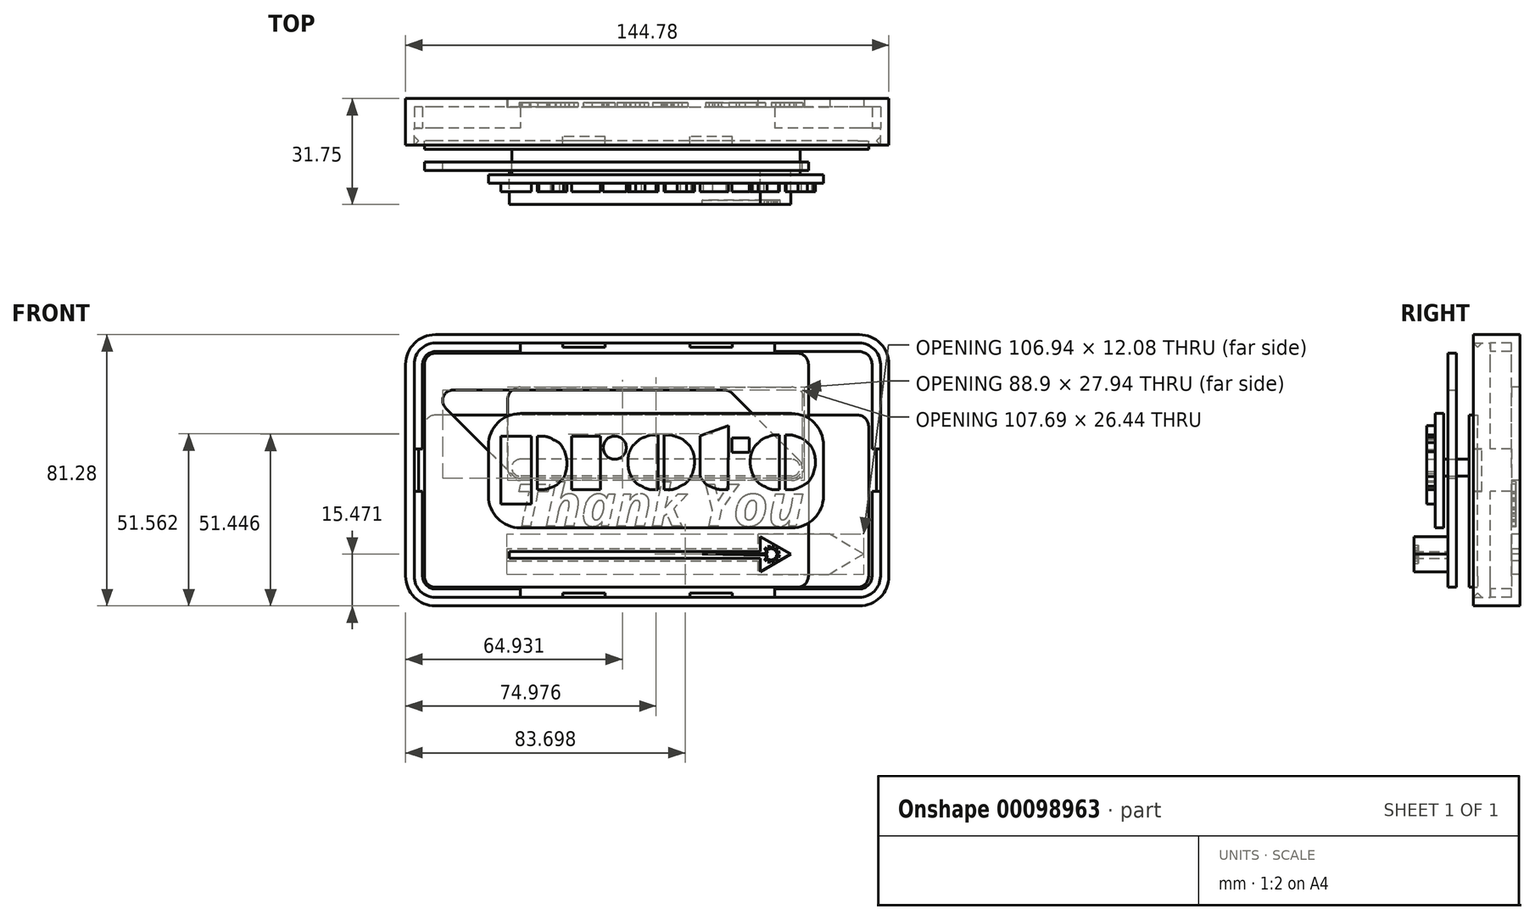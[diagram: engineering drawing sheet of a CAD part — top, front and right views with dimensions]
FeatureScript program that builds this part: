
annotation { "Feature Type Name" : "Feature", "Feature Type Description" : "" }
export const myFeature = defineFeature(function(context is Context, id is Id, definition is map)
    precondition{}
    {
        {
            var Q0;
            Q0=qCreatedBy(makeId("Front.planeOp"),FACE);
            var sketch = newSketch(context, id + "F0", { "sketchPlane" : qUnion([Q0])});
            skLineSegment(sketch, "E0", {"start": v(0, 0) * mm, "end": v(0, 76.06) * mm, "construction": true});
            skLineSegment(sketch, "E1", {"start": v(0, 0) * mm, "end": v(106.57, 0) * mm, "construction": true});
            skLineSegment(sketch, "E2.bottom", {"start": v(63.5, -38.1) * mm, "end": v(-63.5, -38.1) * mm});
            skLineSegment(sketch, "E2.top", {"start": v(63.5, 38.1) * mm, "end": v(-63.5, 38.1) * mm});
            skLineSegment(sketch, "E2.left", {"start": v(69.85, -31.75) * mm, "end": v(69.85, 31.75) * mm});
            skLineSegment(sketch, "E2.right", {"start": v(-69.85, -31.75) * mm, "end": v(-69.85, 31.75) * mm});
            skPoint(sketch, "E3.visualSharp", {"position": v(-69.85, 38.1) * mm});
            skArc(sketch, "E3.filletArc", {"start": v(-63.5, 38.1) * mm, "mid": v(-68, 36.24) * mm, "end": v(-69.85, 31.75) * mm});
            skPoint(sketch, "E4.visualSharp", {"position": v(69.85, 38.1) * mm});
            skArc(sketch, "E4.filletArc", {"start": v(69.85, 31.75) * mm, "mid": v(68, 36.24) * mm, "end": v(63.5, 38.1) * mm});
            skPoint(sketch, "E5.visualSharp", {"position": v(69.85, -38.1) * mm});
            skArc(sketch, "E5.filletArc", {"start": v(63.5, -38.1) * mm, "mid": v(68, -36.24) * mm, "end": v(69.85, -31.75) * mm});
            skPoint(sketch, "E6.visualSharp", {"position": v(-69.85, -38.1) * mm});
            skArc(sketch, "E6.filletArc", {"start": v(-69.85, -31.75) * mm, "mid": v(-68, -36.24) * mm, "end": v(-63.5, -38.1) * mm});
            skSolve(sketch);
        }
        {
            var Q0;
            Q0=makeQuery(id+"F0.imprint","IMPRINT",FACE,{"disambiguationData":[TD([[makeQuery(id+"F0.imprint","IMPRINT",EDGE,{"derivedFrom":sQuery(id+"F0.wireOp",EDGE,"E2.bottom")}),-1.0]])]});
            extrude(context, id + "F1", {"entities" : qUnion([Q0]), "depth" : 2.54 * mm});
        }
        {
            var Q0;
            Q0=makeQuery(id+"F1.opExtrude","CAP_FACE",FACE,{"disambiguationData":[OSD([sQuery(id+"F0.wireOp",EDGE,"E2.bottom"),sQuery(id+"F0.wireOp",EDGE,"E2.top"),sQuery(id+"F0.wireOp",EDGE,"E2.left"),sQuery(id+"F0.wireOp",EDGE,"E2.right"),sQuery(id+"F0.wireOp",EDGE,"E3.filletArc"),sQuery(id+"F0.wireOp",EDGE,"E4.filletArc"),sQuery(id+"F0.wireOp",EDGE,"E5.filletArc"),sQuery(id+"F0.wireOp",EDGE,"E6.filletArc")])],"isStart":false});
            var sketch = newSketch(context, id + "F2", { "sketchPlane" : qUnion([Q0])});
            skArc(sketch, "E7.0", {"start": v(67.31, 31.75) * mm, "mid": v(66.2, 34.44) * mm, "end": v(63.5, 35.56) * mm});
            skLineSegment(sketch, "E7.1", {"start": v(67.3, -31.75) * mm, "end": v(67.31, 31.75) * mm});
            skLineSegment(sketch, "E7.2", {"start": v(63.5, 35.56) * mm, "end": v(-63.5, 35.56) * mm});
            skArc(sketch, "E7.3", {"start": v(63.5, -35.56) * mm, "mid": v(66.2, -34.44) * mm, "end": v(67.3, -31.75) * mm});
            skArc(sketch, "E7.4", {"start": v(-63.5, 35.56) * mm, "mid": v(-66.2, 34.44) * mm, "end": v(-67.31, 31.75) * mm});
            skLineSegment(sketch, "E7.5", {"start": v(-67.31, -31.75) * mm, "end": v(-67.31, 31.75) * mm});
            skArc(sketch, "E7.6", {"start": v(-67.31, -31.75) * mm, "mid": v(-66.2, -34.44) * mm, "end": v(-63.5, -35.56) * mm});
            skLineSegment(sketch, "E7.7", {"start": v(63.5, -35.56) * mm, "end": v(-63.5, -35.56) * mm});
            skSolve(sketch);
        }
        {
            var Q0;
            Q0=makeQuery(id+"F2.imprint","IMPRINT",FACE,{"disambiguationData":[TD([[makeQuery(id+"F2.imprint","IMPRINT",EDGE,{"derivedFrom":sQuery(id+"F2.wireOp",EDGE,"E7.0")}),-1.0]])]});
            extrude(context, id + "F3", {"entities" : qUnion([Q0]), "operationType" : NewBodyOperationType.ADD, "depth" : 6.35 * mm});
        }
        {
            var Q0;
            Q0=qCreatedBy(makeId("Front.planeOp"),FACE);
            cPlane(context, id + "F4", {"entities" : qUnion([Q0]), "cplaneType" : CPlaneType.OFFSET, "offset" : 19.05 * mm, "width" : 152.4 * mm, "height" : 152.4 * mm});
        }
        {
            var Q0;
            Q0=qCreatedBy(id+"F4.planeOp",FACE);
            var sketch = newSketch(context, id + "F5", { "sketchPlane" : qUnion([Q0])});
            skLineSegment(sketch, "E8.0", {"start": v(44.96, -35.05) * mm, "end": v(-63.5, -35.05) * mm});
            skLineSegment(sketch, "E8.1", {"start": v(44.96, 35.05) * mm, "end": v(-63.5, 35.05) * mm});
            skArc(sketch, "E8.2", {"start": v(-63.5, 35.05) * mm, "mid": v(-65.83, 34.08) * mm, "end": v(-66.8, 31.75) * mm});
            skLineSegment(sketch, "E8.3", {"start": v(-66.8, -31.75) * mm, "end": v(-66.8, 31.75) * mm});
            skArc(sketch, "E8.4", {"start": v(-66.8, -31.75) * mm, "mid": v(-65.83, -34.08) * mm, "end": v(-63.5, -35.05) * mm});
            skLineSegment(sketch, "E9", {"start": v(48.26, 31.75) * mm, "end": v(48.26, -31.75) * mm});
            skPoint(sketch, "E10.visualSharp", {"position": v(48.26, 35.05) * mm});
            skArc(sketch, "E10.filletArc", {"start": v(48.26, 31.75) * mm, "mid": v(47.3, 34.08) * mm, "end": v(44.96, 35.05) * mm});
            skPoint(sketch, "E11.visualSharp", {"position": v(48.26, -35.05) * mm});
            skArc(sketch, "E11.filletArc", {"start": v(44.96, -35.05) * mm, "mid": v(47.3, -34.08) * mm, "end": v(48.26, -31.75) * mm});
            skLineSegment(sketch, "E12.left", {"start": v(-41.4, -26.43) * mm, "end": v(-41.4, -24.31) * mm});
            skPoint(sketch, "E13.endSnap0", {"position": v(48.26, 0) * mm});
            skLineSegment(sketch, "E14", {"start": v(-60.39, 18.6) * mm, "end": v(-40.3, -1.48) * mm});
            skLineSegment(sketch, "E15", {"start": v(-35.8, 3) * mm, "end": v(-55.9, 23.1) * mm});
            skArc(sketch, "E16", {"start": v(-40.3, -1.48) * mm, "mid": v(-35.8, -1.48) * mm, "end": v(-35.8, 3) * mm});
            skLineSegment(sketch, "E17.1.0.1", {"start": v(-15.49, 3) * mm, "end": v(-35.58, 23.1) * mm});
            skArc(sketch, "E17.1.0.3", {"start": v(-19.98, -1.48) * mm, "mid": v(-15.49, -1.48) * mm, "end": v(-15.49, 3) * mm});
            skLineSegment(sketch, "E17.1.0.6", {"start": v(-40.07, 18.6) * mm, "end": v(-19.98, -1.48) * mm});
            skLineSegment(sketch, "E17.2.0.1", {"start": v(4.83, 3) * mm, "end": v(-15.26, 23.1) * mm});
            skArc(sketch, "E17.2.0.3", {"start": v(0.34, -1.48) * mm, "mid": v(4.83, -1.48) * mm, "end": v(4.83, 3) * mm});
            skLineSegment(sketch, "E17.2.0.6", {"start": v(-19.75, 18.6) * mm, "end": v(0.34, -1.48) * mm});
            skLineSegment(sketch, "E18.1.3.0", {"start": v(25.15, 3) * mm, "end": v(5.06, 23.1) * mm});
            skArc(sketch, "E18.7.3.0", {"start": v(20.66, -1.48) * mm, "mid": v(25.15, -1.48) * mm, "end": v(25.15, 3) * mm});
            skLineSegment(sketch, "E18.15.3.0", {"start": v(0.57, 18.6) * mm, "end": v(20.66, -1.48) * mm});
            skLineSegment(sketch, "E18.1.4.0", {"start": v(45.47, 3) * mm, "end": v(25.38, 23.1) * mm});
            skArc(sketch, "E18.7.4.0", {"start": v(40.98, -1.48) * mm, "mid": v(45.47, -1.48) * mm, "end": v(45.47, 3) * mm});
            skLineSegment(sketch, "E18.15.4.0", {"start": v(20.9, 18.6) * mm, "end": v(40.98, -1.48) * mm});
            skArc(sketch, "E19", {"start": v(-55.9, 23.1) * mm, "mid": v(-60.39, 23.1) * mm, "end": v(-60.39, 18.6) * mm});
            skArc(sketch, "E20", {"start": v(-35.58, 23.1) * mm, "mid": v(-40.07, 23.1) * mm, "end": v(-40.07, 18.6) * mm});
            skArc(sketch, "E21", {"start": v(-15.26, 23.1) * mm, "mid": v(-19.75, 23.1) * mm, "end": v(-19.75, 18.6) * mm});
            skArc(sketch, "E22", {"start": v(5.06, 23.1) * mm, "mid": v(0.57, 23.1) * mm, "end": v(0.57, 18.6) * mm});
            skArc(sketch, "E23", {"start": v(25.38, 23.1) * mm, "mid": v(20.9, 23.1) * mm, "end": v(20.9, 18.6) * mm});
            skLineSegment(sketch, "E24", {"start": v(33.8, -30.45) * mm, "end": v(33.8, -26.43) * mm});
            skLineSegment(sketch, "E25", {"start": v(33.8, -26.43) * mm, "end": v(-41.4, -26.43) * mm});
            skLineSegment(sketch, "E26", {"start": v(-41.4, -24.31) * mm, "end": v(33.8, -24.31) * mm});
            skLineSegment(sketch, "E27", {"start": v(33.8, -24.31) * mm, "end": v(33.8, -19.9) * mm});
            skLineSegment(sketch, "E28", {"start": v(33.8, -19.9) * mm, "end": v(42.93, -25.17) * mm});
            skLineSegment(sketch, "E29", {"start": v(42.93, -25.17) * mm, "end": v(33.8, -30.45) * mm});
            skLineSegment(sketch, "E30", {"start": v(38.49, -25.17) * mm, "end": v(39.78, -24.46) * mm});
            skLineSegment(sketch, "E31", {"start": v(39.78, -24.46) * mm, "end": v(38.3, -24.48) * mm});
            skLineSegment(sketch, "E32", {"start": v(38.3, -24.48) * mm, "end": v(39.07, -23.21) * mm});
            skLineSegment(sketch, "E33", {"start": v(39.07, -23.21) * mm, "end": v(37.8, -23.97) * mm});
            skLineSegment(sketch, "E34", {"start": v(37.8, -23.97) * mm, "end": v(37.82, -22.5) * mm});
            skLineSegment(sketch, "E35", {"start": v(37.82, -22.5) * mm, "end": v(37.1, -23.78) * mm});
            skLineSegment(sketch, "E36", {"start": v(37.1, -23.78) * mm, "end": v(36.39, -22.49) * mm});
            skLineSegment(sketch, "E37", {"start": v(36.39, -22.49) * mm, "end": v(36.41, -23.97) * mm});
            skLineSegment(sketch, "E38", {"start": v(36.41, -23.97) * mm, "end": v(35.14, -23.2) * mm});
            skLineSegment(sketch, "E39", {"start": v(35.14, -23.2) * mm, "end": v(35.9, -24.47) * mm});
            skLineSegment(sketch, "E40", {"start": v(35.9, -24.47) * mm, "end": v(36.14, -24.84) * mm});
            skLineSegment(sketch, "E41", {"start": v(36.14, -24.84) * mm, "end": v(35.15, -24.85) * mm});
            skLineSegment(sketch, "E42", {"start": v(35.15, -24.85) * mm, "end": v(16.42, -25.17) * mm});
            skLineSegment(sketch, "E43", {"start": v(16.42, -25.17) * mm, "end": v(35.13, -25.5) * mm});
            skLineSegment(sketch, "E44", {"start": v(35.13, -25.5) * mm, "end": v(36.12, -25.5) * mm});
            skLineSegment(sketch, "E45", {"start": v(36.12, -25.5) * mm, "end": v(35.9, -25.86) * mm});
            skLineSegment(sketch, "E46", {"start": v(35.9, -25.86) * mm, "end": v(35.14, -27.13) * mm});
            skLineSegment(sketch, "E47", {"start": v(35.14, -27.13) * mm, "end": v(36.4, -26.37) * mm});
            skLineSegment(sketch, "E48", {"start": v(36.4, -26.37) * mm, "end": v(36.38, -27.85) * mm});
            skLineSegment(sketch, "E49", {"start": v(36.38, -27.85) * mm, "end": v(37.1, -26.56) * mm});
            skLineSegment(sketch, "E50", {"start": v(37.1, -26.56) * mm, "end": v(37.81, -27.85) * mm});
            skLineSegment(sketch, "E51", {"start": v(37.81, -27.85) * mm, "end": v(37.8, -26.37) * mm});
            skLineSegment(sketch, "E52", {"start": v(37.8, -26.37) * mm, "end": v(39.06, -27.14) * mm});
            skLineSegment(sketch, "E53", {"start": v(39.06, -27.14) * mm, "end": v(38.3, -25.87) * mm});
            skLineSegment(sketch, "E54", {"start": v(38.3, -25.87) * mm, "end": v(39.78, -25.9) * mm});
            skLineSegment(sketch, "E55", {"start": v(39.78, -25.9) * mm, "end": v(38.49, -25.17) * mm});
            skLineSegment(sketch, "E56", {"start": v(-58.14, 20.85) * mm, "end": v(-58.14, 24.03) * mm, "construction": true});
            skLineSegment(sketch, "E57", {"start": v(23.14, 20.85) * mm, "end": v(23.14, 24.03) * mm, "construction": true});
            skLineSegment(sketch, "E58", {"start": v(43.23, 0.76) * mm, "end": v(43.23, -2.41) * mm, "construction": true});
            skLineSegment(sketch, "E59", {"start": v(-38.05, 0.76) * mm, "end": v(-38.05, -2.41) * mm, "construction": true});
            skLineSegment(sketch, "E60", {"start": v(-58.14, 24.03) * mm, "end": v(23.14, 24.03) * mm});
            skLineSegment(sketch, "E61", {"start": v(43.23, -2.41) * mm, "end": v(-38.05, -2.41) * mm});
            skSolve(sketch);
        }
        {
            var Q0;
            Q0=makeQuery(id+"F5.imprint","IMPRINT",FACE,{"disambiguationData":[TD([[makeQuery(id+"F5.imprint","IMPRINT",EDGE,{"derivedFrom":sQuery(id+"F5.wireOp",EDGE,"E8.0")}),-1.0]])]});
            var Q1;
            Q1=makeQuery(id+"F5.imprint","IMPRINT",FACE,{"disambiguationData":[TD([[makeQuery(id+"F5.imprint","IMPRINT",EDGE,{"derivedFrom":sQuery(id+"F5.wireOp",EDGE,"E12.bottom")}),1.0]])]});
            var Q2;
            {var subQ0=sQuery(id+"F5.wireOp",EDGE,"RONYQzmz-jIdt-ileG-3skQ-5Jk7ZL3AeCge");Q2=makeQuery(id+"F5.imprint","IMPRINT",FACE,{"disambiguationData":[TD([[makeQuery(id+"F5.imprint","IMPRINT",EDGE,{"derivedFrom":subQ0}),-1.0]])]});}
            var Q3;
            {var subQ1=sQuery(id+"F5.wireOp",EDGE,"E17.1.0.2");Q3=makeQuery(id+"F5.imprint","IMPRINT",FACE,{"disambiguationData":[TD([[makeQuery(id+"F5.imprint","IMPRINT",EDGE,{"derivedFrom":subQ1}),-1.0]])]});}
            var Q4;
            {var subQ1=sQuery(id+"F5.wireOp",EDGE,"E17.2.0.2");Q4=makeQuery(id+"F5.imprint","IMPRINT",FACE,{"disambiguationData":[TD([[makeQuery(id+"F5.imprint","IMPRINT",EDGE,{"derivedFrom":subQ1}),-1.0]])]});}
            var Q5;
            {var subQ1=sQuery(id+"F5.wireOp",EDGE,"E18.4.3.0");Q5=makeQuery(id+"F5.imprint","IMPRINT",FACE,{"disambiguationData":[TD([[makeQuery(id+"F5.imprint","IMPRINT",EDGE,{"derivedFrom":subQ1}),-1.0]])]});}
            var Q6;
            {var subQ1=sQuery(id+"F5.wireOp",EDGE,"E18.4.4.0");Q6=makeQuery(id+"F5.imprint","IMPRINT",FACE,{"disambiguationData":[TD([[makeQuery(id+"F5.imprint","IMPRINT",EDGE,{"derivedFrom":subQ1}),-1.0]])]});}
            var Q7;
            Q7=makeQuery(id+"F5.imprint","IMPRINT",FACE,{"disambiguationData":[TD([[makeQuery(id+"F5.imprint","IMPRINT",EDGE,{"derivedFrom":sQuery(id+"F5.wireOp",EDGE,"E12.right")}),-1.0]])]});
            extrude(context, id + "F6", {"entities" : qUnion([Q0, Q1, Q2, Q3, Q4, Q5, Q6, Q7]), "depth" : 2.54 * mm});
        }
        {
            var Q0;
            Q0=makeQuery(id+"F5.imprint","IMPRINT",FACE,{"disambiguationData":[TD([[makeQuery(id+"F5.imprint","IMPRINT",EDGE,{"derivedFrom":sQuery(id+"F5.wireOp",EDGE,"E12.left")}),-1.0]])]});
            var Q1;
            Q1=makeQuery(id+"F5.imprint","IMPRINT",FACE,{"disambiguationData":[TD([[makeQuery(id+"F5.imprint","IMPRINT",EDGE,{"derivedFrom":sQuery(id+"F5.wireOp",EDGE,"E30")}),1.0]])]});
            extrude(context, id + "F7", {"entities" : qUnion([Q0, Q1]), "operationType" : NewBodyOperationType.ADD, "depth" : 12.7 * mm});
        }
        {
            var Q0;
            Q0=makeQuery(id+"F5.imprint","IMPRINT",FACE,{"disambiguationData":[TD([[makeQuery(id+"F5.imprint","IMPRINT",EDGE,{"derivedFrom":sQuery(id+"F5.wireOp",EDGE,"E30")}),1.0]])]});
            extrude(context, id + "F8", {"entities" : qUnion([Q0]), "operationType" : NewBodyOperationType.REMOVE, "endBound" : BoundingType.THROUGH_ALL, "depth" : 37.6 * mm, "hasSecondDirection" : true, "secondDirectionOppositeDirection" : false, "secondDirectionDepth" : 11.43 * mm});
        }
        {
            var Q0;
            Q0=qCreatedBy(makeId("Front.planeOp"),FACE);
            cPlane(context, id + "F9", {"entities" : qUnion([Q0]), "cplaneType" : CPlaneType.OFFSET, "offset" : 12.7 * mm, "width" : 152.4 * mm, "height" : 152.4 * mm});
        }
        {
            var Q0;
            Q0=qCreatedBy(id+"F9.planeOp",FACE);
            var sketch = newSketch(context, id + "F10", { "sketchPlane" : qUnion([Q0])});
            skLineSegment(sketch, "E62.0", {"start": v(-66.8, -31.75) * mm, "end": v(-66.8, 13.2) * mm});
            skLineSegment(sketch, "E62.1", {"start": v(63, -35.05) * mm, "end": v(-63.5, -35.05) * mm});
            skLineSegment(sketch, "E62.2", {"start": v(66.3, -31.75) * mm, "end": v(66.3, 13.2) * mm});
            skLineSegment(sketch, "E63", {"start": v(63, 16.5) * mm, "end": v(-63.5, 16.51) * mm});
            skArc(sketch, "E64.filletArc", {"start": v(-63.5, 16.51) * mm, "mid": v(-65.83, 15.54) * mm, "end": v(-66.8, 13.2) * mm});
            skArc(sketch, "E65.filletArc", {"start": v(66.3, 13.2) * mm, "mid": v(65.33, 15.54) * mm, "end": v(63, 16.5) * mm});
            skCircle(sketch, "E66", {"center": v(-38.05, 0.76) * mm, "radius": 2.54 * mm});
            skArc(sketch, "E67.0", {"start": v(-66.8, -31.75) * mm, "mid": v(-65.83, -34.08) * mm, "end": v(-63.5, -35.05) * mm});
            skPoint(sketch, "E68.visualSharp", {"position": v(66.3, -35.05) * mm});
            skArc(sketch, "E68.filletArc", {"start": v(63, -35.05) * mm, "mid": v(65.33, -34.08) * mm, "end": v(66.3, -31.75) * mm});
            skCircle(sketch, "E69", {"center": v(43.23, 0.76) * mm, "radius": 2.54 * mm});
            skLineSegment(sketch, "E70", {"start": v(-38.05, 3.3) * mm, "end": v(43.23, 3.3) * mm});
            skLineSegment(sketch, "E71", {"start": v(-38.05, -1.78) * mm, "end": v(43.23, -1.78) * mm});
            skSolve(sketch);
        }
        {
            var Q0;
            Q0=makeQuery(id+"F10.imprint","IMPRINT",FACE,{"disambiguationData":[TD([[makeQuery(id+"F10.imprint","IMPRINT",EDGE,{"derivedFrom":sQuery(id+"F10.wireOp",EDGE,"E62.0")}),-1.0]])]});
            var Q1;
            {var subQ0=sQuery(id+"F10.wireOp",EDGE,"E70");Q1=makeQuery(id+"F10.imprint","IMPRINT",FACE,{"disambiguationData":[TD([[makeQuery(id+"F10.imprint","IMPRINT",EDGE,{"derivedFrom":subQ0}),-1.0]])]});}
            var Q2;
            {var subQ0=sQuery(id+"F10.wireOp",EDGE,"E66");var subQ1=makeQuery(id+"F10.imprint","INTERSECT",VERTEX,{"derivedFrom":[subQ0,sQuery(id+"F10.wireOp",EDGE,"E70")]});Q2=makeQuery(id+"F10.imprint","IMPRINT",FACE,{"disambiguationData":[TD([[makeQuery(id+"F10.imprint","IMPRINT",EDGE,{"disambiguationData":[TD([[subQ1,-1.0]])],"derivedFrom":subQ0}),1.0]])]});}
            var Q3;
            {var subQ0=sQuery(id+"F10.wireOp",EDGE,"E69");var subQ1=makeQuery(id+"F10.imprint","INTERSECT",VERTEX,{"derivedFrom":[subQ0,sQuery(id+"F10.wireOp",EDGE,"E70")]});Q3=makeQuery(id+"F10.imprint","IMPRINT",FACE,{"disambiguationData":[TD([[makeQuery(id+"F10.imprint","IMPRINT",EDGE,{"disambiguationData":[TD([[subQ1,-1.0]])],"derivedFrom":subQ0}),1.0]])]});}
            extrude(context, id + "F11", {"entities" : qUnion([Q0, Q1, Q2, Q3]), "depth" : 2.54 * mm, "offsetDistance" : 25.4 * mm});
        }
        {
            var Q0;
            {var subQ0=sQuery(id+"F10.wireOp",EDGE,"E70");Q0=makeQuery(id+"F10.imprint","IMPRINT",FACE,{"disambiguationData":[TD([[makeQuery(id+"F10.imprint","IMPRINT",EDGE,{"derivedFrom":subQ0}),-1.0]])]});}
            var Q1;
            {var subQ0=sQuery(id+"F10.wireOp",EDGE,"E69");var subQ1=makeQuery(id+"F10.imprint","INTERSECT",VERTEX,{"derivedFrom":[subQ0,sQuery(id+"F10.wireOp",EDGE,"E70")]});Q1=makeQuery(id+"F10.imprint","IMPRINT",FACE,{"disambiguationData":[TD([[makeQuery(id+"F10.imprint","IMPRINT",EDGE,{"disambiguationData":[TD([[subQ1,-1.0]])],"derivedFrom":subQ0}),1.0]])]});}
            var Q2;
            {var subQ0=sQuery(id+"F10.wireOp",EDGE,"E66");var subQ1=makeQuery(id+"F10.imprint","INTERSECT",VERTEX,{"derivedFrom":[subQ0,sQuery(id+"F10.wireOp",EDGE,"E70")]});Q2=makeQuery(id+"F10.imprint","IMPRINT",FACE,{"disambiguationData":[TD([[makeQuery(id+"F10.imprint","IMPRINT",EDGE,{"disambiguationData":[TD([[subQ1,-1.0]])],"derivedFrom":subQ0}),1.0]])]});}
            extrude(context, id + "F12", {"entities" : qUnion([Q0, Q1, Q2]), "operationType" : NewBodyOperationType.ADD, "depth" : 10.16 * mm, "offsetDistance" : 25.4 * mm});
        }
        {
            var Q0;
            Q0=makeQuery(id+"F12.opExtrude","CAP_FACE",FACE,{"disambiguationData":[OSD([sQuery(id+"F10.wireOp",EDGE,"E66")])],"isStart":false});
            var sketch = newSketch(context, id + "F13", { "sketchPlane" : qUnion([Q0])});
            skArc(sketch, "E72", {"start": v(-38.05, 17.02) * mm, "mid": v(-44.79, 14.23) * mm, "end": v(-47.58, 7.5) * mm});
            skLineSegment(sketch, "E73", {"start": v(-47.58, 7.5) * mm, "end": v(-28.53, 7.5) * mm, "construction": true});
            skLineSegment(sketch, "E74", {"start": v(-47.58, -7.75) * mm, "end": v(-47.58, 7.5) * mm});
            skArc(sketch, "E75", {"start": v(-47.58, -7.75) * mm, "mid": v(-44.79, -14.48) * mm, "end": v(-38.05, -17.27) * mm});
            skArc(sketch, "E76", {"start": v(52.75, 7.5) * mm, "mid": v(49.96, 14.23) * mm, "end": v(43.23, 17.02) * mm});
            skLineSegment(sketch, "E77", {"start": v(52.75, 7.5) * mm, "end": v(52.75, -7.75) * mm});
            skArc(sketch, "E78", {"start": v(43.23, -17.27) * mm, "mid": v(49.96, -14.48) * mm, "end": v(52.75, -7.75) * mm});
            skLineSegment(sketch, "E79", {"start": v(-38.05, 17.02) * mm, "end": v(43.23, 17.02) * mm});
            skLineSegment(sketch, "E80", {"start": v(-38.05, -17.27) * mm, "end": v(43.23, -17.27) * mm});
            skSolve(sketch);
        }
        {
            var Q0;
            {var subQ2=sQuery(id+"F13.wireOp",EDGE,"184792f2-019b-4fa7-9458-c084a680c1f6.sketch_text.stroke-0");Q0=makeQuery(id+"F13.imprint","IMPRINT",FACE,{"disambiguationData":[TD([[makeQuery(id+"F13.imprint","IMPRINT",EDGE,{"derivedFrom":subQ2}),1.0]])]});}
            var Q1;
            {var subQ2=sQuery(id+"F13.wireOp",EDGE,"184792f2-019b-4fa7-9458-c084a680c1f6.sketch_text.stroke-0");Q1=makeQuery(id+"F13.imprint","IMPRINT",FACE,{"disambiguationData":[TD([[makeQuery(id+"F13.imprint","IMPRINT",EDGE,{"derivedFrom":subQ2}),-1.0]])]});}
            var Q2;
            {var subQ1=sQuery(id+"F13.wireOp",EDGE,"184792f2-019b-4fa7-9458-c084a680c1f6.sketch_text.stroke-3");Q2=makeQuery(id+"F13.imprint","IMPRINT",FACE,{"disambiguationData":[TD([[makeQuery(id+"F13.imprint","IMPRINT",EDGE,{"derivedFrom":subQ1}),1.0]])]});}
            var Q3;
            {var subQ10=sQuery(id+"F13.wireOp",EDGE,"184792f2-019b-4fa7-9458-c084a680c1f6.sketch_text.stroke-3");Q3=makeQuery(id+"F13.imprint","IMPRINT",FACE,{"disambiguationData":[TD([[makeQuery(id+"F13.imprint","IMPRINT",EDGE,{"derivedFrom":subQ10}),-1.0]])]});}
            var Q4;
            {var subQ0=sQuery(id+"F13.wireOp",EDGE,"184792f2-019b-4fa7-9458-c084a680c1f6.sketch_text.stroke-9");Q4=makeQuery(id+"F13.imprint","IMPRINT",FACE,{"disambiguationData":[TD([[makeQuery(id+"F13.imprint","IMPRINT",EDGE,{"derivedFrom":subQ0}),1.0]])]});}
            var Q5;
            Q5=makeQuery(id+"F13.imprint","IMPRINT",FACE,{"disambiguationData":[TD([[makeQuery(id+"F13.imprint","IMPRINT",EDGE,{"derivedFrom":sQuery(id+"F13.wireOp",EDGE,"E72")}),1.0]])]});
            var Q6;
            Q6=makeQuery(id+"F13.imprint","IMPRINT",FACE,{"disambiguationData":[TD([[makeQuery(id+"F13.imprint","IMPRINT",EDGE,{"derivedFrom":sQuery(id+"F13.wireOp",EDGE,"d38c979e-a2ed-44f1-b070-4af635d20e9c")}),1.0]])]});
            var Q7;
            Q7=makeQuery(id+"F13.imprint","IMPRINT",FACE,{"disambiguationData":[TD([[makeQuery(id+"F13.imprint","IMPRINT",EDGE,{"derivedFrom":sQuery(id+"F13.wireOp",EDGE,"0a407777-59e5-4105-bb9b-3a1e0d8dd915")}),1.0]])]});
            var Q8;
            Q8=makeQuery(id+"F13.imprint","IMPRINT",FACE,{"disambiguationData":[TD([[makeQuery(id+"F13.imprint","IMPRINT",EDGE,{"derivedFrom":sQuery(id+"F13.wireOp",EDGE,"69c1cf4b-b8d7-40c4-819d-392773c8632c")}),1.0]])]});
            var Q9;
            Q9=makeQuery(id+"F13.imprint","IMPRINT",FACE,{"disambiguationData":[TD([[makeQuery(id+"F13.imprint","IMPRINT",EDGE,{"derivedFrom":sQuery(id+"F13.wireOp",EDGE,"E76")}),1.0]])]});
            var Q10;
            Q10=makeQuery(id+"F13.imprint","IMPRINT",FACE,{"disambiguationData":[TD([[makeQuery(id+"F13.imprint","IMPRINT",EDGE,{"derivedFrom":makeQuery(id+"F12.opExtrude","CAP_EDGE",EDGE,{"disambiguationData":[OSD([sQuery(id+"F10.wireOp",EDGE,"E66")])],"isStart":false})}),1.0]])]});
            extrude(context, id + "F14", {"entities" : qUnion([Q0, Q1, Q2, Q3, Q4, Q5, Q6, Q7, Q8, Q9, Q10]), "depth" : 2.54 * mm});
        }
        {
            var Q0;
            Q0=makeQuery(id+"F14.opExtrude","CAP_FACE",FACE,{"disambiguationData":[OSD([sQuery(id+"F13.wireOp",EDGE,"E72"),sQuery(id+"F13.wireOp",EDGE,"E74"),sQuery(id+"F13.wireOp",EDGE,"E75"),sQuery(id+"F13.wireOp",EDGE,"E76"),sQuery(id+"F13.wireOp",EDGE,"E77"),sQuery(id+"F13.wireOp",EDGE,"E78"),sQuery(id+"F13.wireOp",EDGE,"E79"),sQuery(id+"F13.wireOp",EDGE,"E80")])],"isStart":false});
            var sketch = newSketch(context, id + "F15", { "sketchPlane" : qUnion([Q0])});
            skFitSpline(sketch, "E81", {"points": [v(39.38, -5.83) * mm, v(37.77, -5.83) * mm, v(36.3, -5.44) * mm, v(34.96, -4.73) * mm]});
            skFitSpline(sketch, "E82", {"points": [v(34.96, -4.73) * mm, v(33.65, -4.03) * mm, v(32.6, -3.04) * mm, v(31.84, -1.8) * mm]});
            skFitSpline(sketch, "E83", {"points": [v(31.34, 5.54) * mm, v(31.77, 6.52) * mm, v(32.38, 7.39) * mm, v(33.18, 8.15) * mm]});
            skFitSpline(sketch, "E84", {"points": [v(33.18, 8.15) * mm, v(33.98, 8.9) * mm, v(34.9, 9.54) * mm, v(35.93, 9.94) * mm]});
            skFitSpline(sketch, "E85", {"points": [v(35.93, 9.94) * mm, v(36.98, 10.34) * mm, v(38.1, 10.6) * mm, v(39.29, 10.6) * mm]});
            skFitSpline(sketch, "E86", {"points": [v(41.6, 10.6) * mm, v(42.9, 10.6) * mm, v(44.1, 10.35) * mm, v(45.18, 9.95) * mm]});
            skFitSpline(sketch, "E87", {"points": [v(45.18, 9.95) * mm, v(46.28, 9.55) * mm, v(47.22, 8.96) * mm, v(47.98, 8.24) * mm]});
            skFitSpline(sketch, "E88", {"points": [v(47.98, 8.24) * mm, v(48.78, 7.5) * mm, v(49.4, 6.62) * mm, v(49.83, 5.61) * mm]});
            skFitSpline(sketch, "E89", {"points": [v(49.35, -1.81) * mm, v(48.6, -3.04) * mm, v(47.55, -4.04) * mm, v(46.2, -4.75) * mm]});
            skFitSpline(sketch, "E90", {"points": [v(46.2, -4.75) * mm, v(44.87, -5.45) * mm, v(43.36, -5.83) * mm, v(41.68, -5.83) * mm]});
            skLineSegment(sketch, "E91", {"start": v(30.53, 5.41) * mm, "end": v(25.34, 5.41) * mm});
            skLineSegment(sketch, "E92", {"start": v(25.34, 5.41) * mm, "end": v(25.34, 9.74) * mm});
            skLineSegment(sketch, "E93", {"start": v(25.34, 9.74) * mm, "end": v(30.53, 9.74) * mm});
            skLineSegment(sketch, "E94", {"start": v(30.53, 9.74) * mm, "end": v(30.53, 5.41) * mm});
            skFitSpline(sketch, "E95", {"points": [v(5.35, 10.6) * mm, v(6.66, 10.6) * mm, v(7.85, 10.35) * mm, v(8.93, 9.95) * mm]});
            skFitSpline(sketch, "E96", {"points": [v(8.93, 9.95) * mm, v(10.03, 9.55) * mm, v(10.97, 8.96) * mm, v(11.73, 8.24) * mm]});
            skFitSpline(sketch, "E97", {"points": [v(11.73, 8.24) * mm, v(12.52, 7.5) * mm, v(13.14, 6.62) * mm, v(13.58, 5.61) * mm]});
            skFitSpline(sketch, "E98", {"points": [v(13.1, -1.81) * mm, v(12.35, -3.04) * mm, v(11.3, -4.04) * mm, v(9.95, -4.75) * mm]});
            skFitSpline(sketch, "E99", {"points": [v(9.95, -4.75) * mm, v(8.62, -5.45) * mm, v(7.1, -5.83) * mm, v(5.43, -5.83) * mm]});
            skFitSpline(sketch, "E100", {"points": [v(2.7, -5.83) * mm, v(1.09, -5.83) * mm, v(-0.39, -5.44) * mm, v(-1.72, -4.73) * mm]});
            skFitSpline(sketch, "E101", {"points": [v(-1.72, -4.73) * mm, v(-3.04, -4.03) * mm, v(-4.08, -3.04) * mm, v(-4.84, -1.8) * mm]});
            skFitSpline(sketch, "E102", {"points": [v(-5.34, 5.54) * mm, v(-4.92, 6.52) * mm, v(-4.3, 7.39) * mm, v(-3.5, 8.15) * mm]});
            skFitSpline(sketch, "E103", {"points": [v(-3.5, 8.15) * mm, v(-2.7, 8.9) * mm, v(-1.79, 9.54) * mm, v(-0.75, 9.94) * mm]});
            skFitSpline(sketch, "E104", {"points": [v(-0.75, 9.94) * mm, v(0.3, 10.34) * mm, v(1.41, 10.6) * mm, v(2.6, 10.6) * mm]});
            skFitSpline(sketch, "E105", {"points": [v(-32.57, 10.17) * mm, v(-31, 10.17) * mm, v(-29.54, 9.9) * mm, v(-28.2, 9.18) * mm]});
            skFitSpline(sketch, "E106", {"points": [v(-28.2, 9.18) * mm, v(-26.88, 8.48) * mm, v(-25.83, 7.55) * mm, v(-25.07, 6.3) * mm]});
            skFitSpline(sketch, "E107", {"points": [v(-24.53, -0.97) * mm, v(-24.93, -1.95) * mm, v(-25.5, -2.79) * mm, v(-26.23, -3.5) * mm]});
            skFitSpline(sketch, "E108", {"points": [v(-26.23, -3.5) * mm, v(-26.97, -4.24) * mm, v(-27.85, -4.79) * mm, v(-28.88, -5.18) * mm]});
            skFitSpline(sketch, "E109", {"points": [v(-28.88, -5.18) * mm, v(-29.9, -5.57) * mm, v(-31, -5.77) * mm, v(-32.22, -5.77) * mm]});
            skLineSegment(sketch, "E110", {"start": v(-43.83, -10.15) * mm, "end": v(-43.83, 10.17) * mm});
            skLineSegment(sketch, "E111", {"start": v(-43.83, 10.17) * mm, "end": v(-34.75, 10.17) * mm});
            skLineSegment(sketch, "E112", {"start": v(-34.75, 10.17) * mm, "end": v(-34.75, -10.15) * mm});
            skLineSegment(sketch, "E113", {"start": v(-34.75, -10.15) * mm, "end": v(-43.83, -10.15) * mm});
            skLineSegment(sketch, "E114", {"start": v(-14, -5.83) * mm, "end": v(-22.65, -5.83) * mm});
            skLineSegment(sketch, "E115", {"start": v(-22.65, -5.83) * mm, "end": v(-22.65, 10.17) * mm});
            skLineSegment(sketch, "E116", {"start": v(-22.65, 10.17) * mm, "end": v(-14, 10.17) * mm});
            skLineSegment(sketch, "E117", {"start": v(-14, 10.17) * mm, "end": v(-14, -5.83) * mm});
            skFitSpline(sketch, "E118", {"points": [v(23.68, -5.83) * mm, v(22.16, -5.83) * mm, v(20.8, -5.6) * mm, v(19.58, -5.12) * mm]});
            skFitSpline(sketch, "E119", {"points": [v(19.58, -5.12) * mm, v(18.33, -4.64) * mm, v(17.45, -4) * mm, v(16.79, -3.17) * mm]});
            skFitSpline(sketch, "E120", {"points": [v(16.79, -3.17) * mm, v(16.1, -2.34) * mm, v(15.83, -1.42) * mm, v(15.83, -0.4) * mm]});
            skLineSegment(sketch, "E121", {"start": v(15.83, -0.4) * mm, "end": v(15.83, 10.32) * mm});
            skLineSegment(sketch, "E122", {"start": v(15.83, 10.32) * mm, "end": v(24.33, 13.39) * mm});
            skLineSegment(sketch, "E123", {"start": v(24.33, 13.39) * mm, "end": v(24.23, -5.83) * mm});
            skLineSegment(sketch, "E124", {"start": v(24.23, -5.83) * mm, "end": v(23.68, -5.83) * mm});
            skLineSegment(sketch, "E125", {"start": v(-32.57, 10.17) * mm, "end": v(-33.02, 10.17) * mm});
            skLineSegment(sketch, "E126", {"start": v(-33.02, -5.83) * mm, "end": v(-32.61, -5.83) * mm});
            skLineSegment(sketch, "E127", {"start": v(-33.02, 10.17) * mm, "end": v(-33.02, -5.83) * mm});
            skLineSegment(sketch, "E128", {"start": v(-32.22, -5.77) * mm, "end": v(-32.61, -5.83) * mm});
            skArc(sketch, "E129", {"start": v(-24.53, -0.97) * mm, "mid": v(-24.12, 2.72) * mm, "end": v(-25.07, 6.3) * mm});
            skCircle(sketch, "E130", {"center": v(-9.75, 6.76) * mm, "radius": 3.46 * mm});
            skArc(sketch, "E131", {"start": v(-5.34, 5.54) * mm, "mid": v(-5.82, 1.83) * mm, "end": v(-4.84, -1.8) * mm});
            skArc(sketch, "E132", {"start": v(13.1, -1.81) * mm, "mid": v(14.12, 1.85) * mm, "end": v(13.58, 5.61) * mm});
            skLineSegment(sketch, "E133", {"start": v(3.3, 10.6) * mm, "end": v(3.3, -5.83) * mm});
            skLineSegment(sketch, "E134", {"start": v(5.02, -5.83) * mm, "end": v(5.02, 10.6) * mm});
            skLineSegment(sketch, "E135", {"start": v(2.6, 10.6) * mm, "end": v(3.3, 10.6) * mm});
            skLineSegment(sketch, "E136", {"start": v(5.02, 10.6) * mm, "end": v(5.35, 10.6) * mm});
            skLineSegment(sketch, "E137", {"start": v(2.7, -5.83) * mm, "end": v(3.3, -5.83) * mm});
            skLineSegment(sketch, "E138", {"start": v(5.02, -5.83) * mm, "end": v(5.43, -5.83) * mm});
            skLineSegment(sketch, "E139", {"start": v(39.6, 10.6) * mm, "end": v(39.6, -5.83) * mm});
            skLineSegment(sketch, "E140", {"start": v(41.34, -5.83) * mm, "end": v(41.34, 10.6) * mm});
            skLineSegment(sketch, "E141", {"start": v(39.29, 10.6) * mm, "end": v(39.6, 10.6) * mm});
            skLineSegment(sketch, "E142", {"start": v(41.34, 10.6) * mm, "end": v(41.6, 10.6) * mm});
            skLineSegment(sketch, "E143", {"start": v(39.38, -5.83) * mm, "end": v(39.6, -5.83) * mm});
            skLineSegment(sketch, "E144", {"start": v(41.34, -5.83) * mm, "end": v(41.68, -5.83) * mm});
            skArc(sketch, "E145", {"start": v(31.34, 5.54) * mm, "mid": v(30.83, 1.82) * mm, "end": v(31.84, -1.8) * mm});
            skArc(sketch, "E146", {"start": v(49.35, -1.81) * mm, "mid": v(50.33, 1.85) * mm, "end": v(49.83, 5.61) * mm});
            skSolve(sketch);
        }
        {
            var Q0;
            Q0=makeQuery(id+"F15.imprint","IMPRINT",FACE,{"disambiguationData":[TD([[makeQuery(id+"F15.imprint","IMPRINT",EDGE,{"derivedFrom":sQuery(id+"F15.wireOp",EDGE,"E110")}),-1.0]])]});
            var Q1;
            Q1=makeQuery(id+"F15.imprint","IMPRINT",FACE,{"disambiguationData":[TD([[makeQuery(id+"F15.imprint","IMPRINT",EDGE,{"derivedFrom":sQuery(id+"F15.wireOp",EDGE,"E105")}),-1.0]])]});
            var Q2;
            Q2=makeQuery(id+"F15.imprint","IMPRINT",FACE,{"disambiguationData":[TD([[makeQuery(id+"F15.imprint","IMPRINT",EDGE,{"derivedFrom":sQuery(id+"F15.wireOp",EDGE,"E114")}),-1.0]])]});
            var Q3;
            Q3=makeQuery(id+"F15.imprint","IMPRINT",FACE,{"disambiguationData":[TD([[makeQuery(id+"F15.imprint","IMPRINT",EDGE,{"derivedFrom":sQuery(id+"F15.wireOp",EDGE,"E130")}),1.0]])]});
            var Q4;
            Q4=makeQuery(id+"F15.imprint","IMPRINT",FACE,{"disambiguationData":[TD([[makeQuery(id+"F15.imprint","IMPRINT",EDGE,{"derivedFrom":sQuery(id+"F15.wireOp",EDGE,"E100")}),-1.0]])]});
            var Q5;
            Q5=makeQuery(id+"F15.imprint","IMPRINT",FACE,{"disambiguationData":[TD([[makeQuery(id+"F15.imprint","IMPRINT",EDGE,{"derivedFrom":sQuery(id+"F15.wireOp",EDGE,"E95")}),-1.0]])]});
            var Q6;
            Q6=makeQuery(id+"F15.imprint","IMPRINT",FACE,{"disambiguationData":[TD([[makeQuery(id+"F15.imprint","IMPRINT",EDGE,{"derivedFrom":sQuery(id+"F15.wireOp",EDGE,"E118")}),-1.0]])]});
            var Q7;
            Q7=makeQuery(id+"F15.imprint","IMPRINT",FACE,{"disambiguationData":[TD([[makeQuery(id+"F15.imprint","IMPRINT",EDGE,{"derivedFrom":sQuery(id+"F15.wireOp",EDGE,"E91")}),-1.0]])]});
            var Q8;
            Q8=makeQuery(id+"F15.imprint","IMPRINT",FACE,{"disambiguationData":[TD([[makeQuery(id+"F15.imprint","IMPRINT",EDGE,{"derivedFrom":sQuery(id+"F15.wireOp",EDGE,"E81")}),-1.0]])]});
            var Q9;
            Q9=makeQuery(id+"F15.imprint","IMPRINT",FACE,{"disambiguationData":[TD([[makeQuery(id+"F15.imprint","IMPRINT",EDGE,{"derivedFrom":sQuery(id+"F15.wireOp",EDGE,"E86")}),-1.0]])]});
            extrude(context, id + "F16", {"entities" : qUnion([Q0, Q1, Q2, Q3, Q4, Q5, Q6, Q7, Q8, Q9]), "operationType" : NewBodyOperationType.ADD, "depth" : 2.54 * mm});
        }
        {
            var Q0;
            Q0=makeQuery(id+"F0.imprint","IMPRINT",FACE,{"disambiguationData":[TD([[makeQuery(id+"F0.imprint","IMPRINT",EDGE,{"derivedFrom":sQuery(id+"F0.wireOp",EDGE,"E2.bottom")}),-1.0]])]});
            extrude(context, id + "F17", {"entities" : qUnion([Q0]), "depth" : 2.54 * mm});
        }
        {
            var Q0;
            Q0=makeQuery(id+"F17.opExtrude","CAP_FACE",FACE,{"disambiguationData":[OSD([sQuery(id+"F0.wireOp",EDGE,"E2.bottom"),sQuery(id+"F0.wireOp",EDGE,"E2.top"),sQuery(id+"F0.wireOp",EDGE,"E2.left"),sQuery(id+"F0.wireOp",EDGE,"E2.right"),sQuery(id+"F0.wireOp",EDGE,"E3.filletArc"),sQuery(id+"F0.wireOp",EDGE,"E4.filletArc"),sQuery(id+"F0.wireOp",EDGE,"E5.filletArc"),sQuery(id+"F0.wireOp",EDGE,"E6.filletArc")])],"isStart":false});
            var sketch = newSketch(context, id + "F18", { "sketchPlane" : qUnion([Q0])});
            skCircle(sketch, "E147.0", {"center": v(-38.05, 0.76) * mm, "radius": 2.54 * mm, "construction": true});
            skCircle(sketch, "E148.0", {"center": v(-17.73, 0.76) * mm, "radius": 2.54 * mm, "construction": true});
            skCircle(sketch, "E149.0", {"center": v(2.59, 0.76) * mm, "radius": 2.54 * mm, "construction": true});
            skCircle(sketch, "E150.0", {"center": v(22.9, 0.76) * mm, "radius": 2.54 * mm, "construction": true});
            skCircle(sketch, "E151.0", {"center": v(43.23, 0.76) * mm, "radius": 2.54 * mm, "construction": true});
            skLineSegment(sketch, "E152", {"start": v(-69.85, 0.76) * mm, "end": v(69.85, 0.76) * mm, "construction": true});
            skLineSegment(sketch, "E153", {"start": v(-69.85, 21.08) * mm, "end": v(69.85, 21.08) * mm, "construction": true});
            skArc(sketch, "E154", {"start": v(-41.86, 0.76) * mm, "mid": v(-38.05, -3.05) * mm, "end": v(-34.24, 0.76) * mm});
            skArc(sketch, "E155", {"start": v(-21.54, 0.76) * mm, "mid": v(-17.73, -3.05) * mm, "end": v(-13.92, 0.76) * mm});
            skArc(sketch, "E156", {"start": v(-1.22, 0.76) * mm, "mid": v(2.59, -3.05) * mm, "end": v(6.4, 0.76) * mm});
            skArc(sketch, "E157", {"start": v(19.1, 0.76) * mm, "mid": v(22.9, -3.05) * mm, "end": v(26.72, 0.76) * mm});
            skArc(sketch, "E158", {"start": v(39.42, 0.76) * mm, "mid": v(43.23, -3.05) * mm, "end": v(47.04, 0.76) * mm});
            skLineSegment(sketch, "E159", {"start": v(-41.86, 0.76) * mm, "end": v(-41.86, 21.08) * mm});
            skLineSegment(sketch, "E160", {"start": v(-34.24, 0.76) * mm, "end": v(-34.24, 21.08) * mm});
            skLineSegment(sketch, "E161", {"start": v(-21.54, 0.76) * mm, "end": v(-21.54, 21.08) * mm});
            skLineSegment(sketch, "E162", {"start": v(-13.92, 0.76) * mm, "end": v(-13.92, 21.08) * mm});
            skLineSegment(sketch, "E163", {"start": v(-1.22, 0.76) * mm, "end": v(-1.22, 21.08) * mm});
            skLineSegment(sketch, "E164", {"start": v(6.4, 0.76) * mm, "end": v(6.4, 21.08) * mm});
            skLineSegment(sketch, "E165", {"start": v(19.1, 0.76) * mm, "end": v(19.1, 21.08) * mm});
            skLineSegment(sketch, "E166", {"start": v(26.72, 0.76) * mm, "end": v(26.72, 21.08) * mm});
            skLineSegment(sketch, "E167", {"start": v(39.42, 0.76) * mm, "end": v(39.42, 21.08) * mm});
            skLineSegment(sketch, "E168", {"start": v(47.04, 0.76) * mm, "end": v(47.04, 21.08) * mm});
            skArc(sketch, "E169", {"start": v(-34.24, 21.08) * mm, "mid": v(-38.05, 24.9) * mm, "end": v(-41.86, 21.08) * mm});
            skArc(sketch, "E170", {"start": v(-13.92, 21.08) * mm, "mid": v(-17.73, 24.9) * mm, "end": v(-21.54, 21.08) * mm});
            skArc(sketch, "E171", {"start": v(6.4, 21.08) * mm, "mid": v(2.59, 24.9) * mm, "end": v(-1.22, 21.08) * mm});
            skArc(sketch, "E172", {"start": v(26.72, 21.08) * mm, "mid": v(22.9, 24.9) * mm, "end": v(19.1, 21.08) * mm});
            skArc(sketch, "E173", {"start": v(47.04, 21.08) * mm, "mid": v(43.23, 24.9) * mm, "end": v(39.42, 21.08) * mm});
            skLineSegment(sketch, "E174", {"start": v(33.03, -23.55) * mm, "end": v(-42.16, -23.55) * mm});
            skLineSegment(sketch, "E175", {"start": v(-42.16, -23.55) * mm, "end": v(-42.16, -27.2) * mm});
            skLineSegment(sketch, "E176", {"start": v(-42.16, -27.2) * mm, "end": v(33.03, -27.2) * mm});
            skLineSegment(sketch, "E177", {"start": v(33.03, -27.2) * mm, "end": v(33.03, -31.2) * mm});
            skLineSegment(sketch, "E178", {"start": v(33.03, -31.2) * mm, "end": v(64.78, -31.2) * mm});
            skLineSegment(sketch, "E179", {"start": v(64.78, -31.2) * mm, "end": v(64.78, -19.13) * mm});
            skLineSegment(sketch, "E180", {"start": v(64.78, -19.13) * mm, "end": v(33.03, -19.13) * mm});
            skLineSegment(sketch, "E181", {"start": v(33.03, -19.13) * mm, "end": v(33.03, -23.55) * mm});
            skLineSegment(sketch, "E182", {"start": v(64.78, -25.17) * mm, "end": v(54.62, -19.13) * mm});
            skLineSegment(sketch, "E183", {"start": v(64.78, -25.17) * mm, "end": v(54.62, -31.2) * mm});
            skLineSegment(sketch, "E184", {"start": v(-38.05, 24.9) * mm, "end": v(43.23, 24.9) * mm});
            skLineSegment(sketch, "E185", {"start": v(43.23, -3.05) * mm, "end": v(-38.05, -3.05) * mm});
            skSolve(sketch);
        }
        {
            var Q0;
            Q0=makeQuery(id+"F18.imprint","IMPRINT",FACE,{"disambiguationData":[TD([[makeQuery(id+"F18.imprint","IMPRINT",EDGE,{"derivedFrom":sQuery(id+"F18.wireOp",EDGE,"E154")}),1.0]])]});
            var Q1;
            Q1=makeQuery(id+"F18.imprint","IMPRINT",FACE,{"disambiguationData":[TD([[makeQuery(id+"F18.imprint","IMPRINT",EDGE,{"derivedFrom":sQuery(id+"F18.wireOp",EDGE,"E155")}),1.0]])]});
            var Q2;
            Q2=makeQuery(id+"F18.imprint","IMPRINT",FACE,{"disambiguationData":[TD([[makeQuery(id+"F18.imprint","IMPRINT",EDGE,{"derivedFrom":sQuery(id+"F18.wireOp",EDGE,"E156")}),1.0]])]});
            var Q3;
            Q3=makeQuery(id+"F18.imprint","IMPRINT",FACE,{"disambiguationData":[TD([[makeQuery(id+"F18.imprint","IMPRINT",EDGE,{"derivedFrom":sQuery(id+"F18.wireOp",EDGE,"E157")}),1.0]])]});
            var Q4;
            Q4=makeQuery(id+"F18.imprint","IMPRINT",FACE,{"disambiguationData":[TD([[makeQuery(id+"F18.imprint","IMPRINT",EDGE,{"derivedFrom":sQuery(id+"F18.wireOp",EDGE,"E158")}),1.0]])]});
            var Q5;
            Q5=makeQuery(id+"F18.imprint","IMPRINT",FACE,{"disambiguationData":[TD([[makeQuery(id+"F18.imprint","IMPRINT",EDGE,{"derivedFrom":sQuery(id+"F18.wireOp",EDGE,"E174")}),1.0]])]});
            var Q6;
            {var subQ1=sQuery(id+"F18.wireOp",EDGE,"E160");Q6=makeQuery(id+"F18.imprint","IMPRINT",FACE,{"disambiguationData":[TD([[makeQuery(id+"F18.imprint","IMPRINT",EDGE,{"derivedFrom":subQ1}),-1.0]])]});}
            var Q7;
            {var subQ1=sQuery(id+"F18.wireOp",EDGE,"E162");Q7=makeQuery(id+"F18.imprint","IMPRINT",FACE,{"disambiguationData":[TD([[makeQuery(id+"F18.imprint","IMPRINT",EDGE,{"derivedFrom":subQ1}),-1.0]])]});}
            var Q8;
            {var subQ1=sQuery(id+"F18.wireOp",EDGE,"E164");Q8=makeQuery(id+"F18.imprint","IMPRINT",FACE,{"disambiguationData":[TD([[makeQuery(id+"F18.imprint","IMPRINT",EDGE,{"derivedFrom":subQ1}),-1.0]])]});}
            var Q9;
            {var subQ1=sQuery(id+"F18.wireOp",EDGE,"E166");Q9=makeQuery(id+"F18.imprint","IMPRINT",FACE,{"disambiguationData":[TD([[makeQuery(id+"F18.imprint","IMPRINT",EDGE,{"derivedFrom":subQ1}),-1.0]])]});}
            extrude(context, id + "F19", {"entities" : qUnion([Q0, Q1, Q2, Q3, Q4, Q5, Q6, Q7, Q8, Q9]), "operationType" : NewBodyOperationType.REMOVE, "endBound" : BoundingType.UP_TO_NEXT, "oppositeDirection" : true, "depth" : 25.4 * mm, "offsetDistance" : 25.4 * mm});
        }
        {
            var Q0;
            Q0=makeQuery(id+"F17.opExtrude","CAP_FACE",FACE,{"disambiguationData":[OSD([sQuery(id+"F0.wireOp",EDGE,"E2.bottom"),sQuery(id+"F0.wireOp",EDGE,"E2.top"),sQuery(id+"F0.wireOp",EDGE,"E2.left"),sQuery(id+"F0.wireOp",EDGE,"E2.right"),sQuery(id+"F0.wireOp",EDGE,"E3.filletArc"),sQuery(id+"F0.wireOp",EDGE,"E4.filletArc"),sQuery(id+"F0.wireOp",EDGE,"E5.filletArc"),sQuery(id+"F0.wireOp",EDGE,"E6.filletArc")])],"isStart":false});
            var sketch = newSketch(context, id + "F20", { "sketchPlane" : qUnion([Q0])});
            skText(sketch, "E186", { "text": "Thank You", "fontName": "OpenSans-BoldItalic.ttf"});
            const initialGuessF20  = {"E186": [-0.03988, -0.01676, 1, 0, 0.0127]};
            skSetInitialGuess(sketch, initialGuessF20);
            skSolve(sketch);
        }
        {
            var Q0;
            Q0 = qSketchRegion(id + "F20", true);
            extrude(context, id + "F21", {"entities" : qUnion([Q0]), "operationType" : NewBodyOperationType.REMOVE, "oppositeDirection" : true, "depth" : 1.27 * mm});
        }
        {
            var Q0;
            Q0=qCreatedBy(makeId("Right.planeOp"),FACE);
            var sketch = newSketch(context, id + "F22", { "sketchPlane" : qUnion([Q0])});
            skLineSegment(sketch, "E187.0", {"start": v(-8.9, 38.1) * mm, "end": v(0, 38.1) * mm});
            skLineSegment(sketch, "E188.0", {"start": v(0, 31.75) * mm, "end": v(0, 38.1) * mm});
            skLineSegment(sketch, "E189.0", {"start": v(-8.9, 31.75) * mm, "end": v(-8.9, 38.1) * mm});
            skLineSegment(sketch, "E190", {"start": v(0, 38.1) * mm, "end": v(0, 40.64) * mm});
            skLineSegment(sketch, "E191", {"start": v(0, 40.64) * mm, "end": v(-13.97, 40.64) * mm});
            skLineSegment(sketch, "E192", {"start": v(-13.97, 40.64) * mm, "end": v(-13.97, 38.1) * mm});
            skLineSegment(sketch, "E193", {"start": v(-13.97, 38.1) * mm, "end": v(-12.7, 36.83) * mm});
            skLineSegment(sketch, "E194", {"start": v(-12.7, 36.83) * mm, "end": v(-11.43, 38.1) * mm});
            skLineSegment(sketch, "E195", {"start": v(-11.43, 38.1) * mm, "end": v(-8.9, 38.1) * mm});
            skSolve(sketch);
        }
        {
            var Q0;
            Q0=makeQuery(id+"F1.opExtrude","CAP_FACE",FACE,{"disambiguationData":[OSD([sQuery(id+"F0.wireOp",EDGE,"E2.bottom"),sQuery(id+"F0.wireOp",EDGE,"E2.top"),sQuery(id+"F0.wireOp",EDGE,"E2.left"),sQuery(id+"F0.wireOp",EDGE,"E2.right"),sQuery(id+"F0.wireOp",EDGE,"E3.filletArc"),sQuery(id+"F0.wireOp",EDGE,"E4.filletArc"),sQuery(id+"F0.wireOp",EDGE,"E5.filletArc"),sQuery(id+"F0.wireOp",EDGE,"E6.filletArc")])],"isStart":true});
            var sketch = newSketch(context, id + "F23", { "sketchPlane" : qUnion([Q0])});
            skLineSegment(sketch, "E196", {"start": v(0, 38.1) * mm, "end": v(63.5, 38.1) * mm});
            skArc(sketch, "E197.0", {"start": v(63.5, 38.1) * mm, "mid": v(68, 36.24) * mm, "end": v(69.85, 31.75) * mm});
            skLineSegment(sketch, "E198.0", {"start": v(69.85, -31.75) * mm, "end": v(69.85, 31.75) * mm});
            skArc(sketch, "E199.0", {"start": v(69.85, -31.75) * mm, "mid": v(68, -36.24) * mm, "end": v(63.5, -38.1) * mm});
            skLineSegment(sketch, "E200.0", {"start": v(-63.5, -38.1) * mm, "end": v(63.5, -38.1) * mm});
            skArc(sketch, "E201.0", {"start": v(-63.5, -38.1) * mm, "mid": v(-68, -36.24) * mm, "end": v(-69.85, -31.75) * mm});
            skLineSegment(sketch, "E202.0", {"start": v(-69.85, -31.75) * mm, "end": v(-69.85, 31.75) * mm});
            skArc(sketch, "E203.0", {"start": v(-69.85, 31.75) * mm, "mid": v(-68, 36.24) * mm, "end": v(-63.5, 38.1) * mm});
            skLineSegment(sketch, "E204", {"start": v(-63.5, 38.1) * mm, "end": v(0, 38.1) * mm});
            skSolve(sketch);
        }
        {
            var Q0;
            Q0=makeQuery(id+"F22.imprint","IMPRINT",FACE,{"disambiguationData":[TD([[makeQuery(id+"F22.imprint","IMPRINT",EDGE,{"derivedFrom":sQuery(id+"F22.wireOp",EDGE,"E187.0")}),1.0]])]});
            var Q1;
            Q1 = qConstructionFilter(qBodyType(qCreatedBy(id + "F23" ,EDGE), BodyType.WIRE), ConstructionObject.NO);
            sweep(context, id + "F24", {"operationType" : NewBodyOperationType.ADD, "profiles" : qUnion([Q0]), "path" : qUnion([Q1])});
        }
        {
            var Q0;
            Q0=makeQuery(id+"F3.opExtrude","CAP_FACE",FACE,{"disambiguationData":[OSD([sQuery(id+"F0.wireOp",EDGE,"E2.bottom"),sQuery(id+"F0.wireOp",EDGE,"E2.top"),sQuery(id+"F0.wireOp",EDGE,"E2.left"),sQuery(id+"F0.wireOp",EDGE,"E2.right"),sQuery(id+"F0.wireOp",EDGE,"E3.filletArc"),sQuery(id+"F0.wireOp",EDGE,"E4.filletArc"),sQuery(id+"F0.wireOp",EDGE,"E5.filletArc"),sQuery(id+"F0.wireOp",EDGE,"E6.filletArc"),sQuery(id+"F2.wireOp",EDGE,"E7.0"),sQuery(id+"F2.wireOp",EDGE,"E7.1"),sQuery(id+"F2.wireOp",EDGE,"E7.2"),sQuery(id+"F2.wireOp",EDGE,"E7.3"),sQuery(id+"F2.wireOp",EDGE,"E7.4"),sQuery(id+"F2.wireOp",EDGE,"E7.5"),sQuery(id+"F2.wireOp",EDGE,"E7.6"),sQuery(id+"F2.wireOp",EDGE,"E7.7")])],"isStart":false});
            var sketch = newSketch(context, id + "F25", { "sketchPlane" : qUnion([Q0])});
            skLineSegment(sketch, "E205.0", {"start": v(63.5, 38.1) * mm, "end": v(-63.5, 38.1) * mm});
            skLineSegment(sketch, "E206.0", {"start": v(-69.85, -31.75) * mm, "end": v(-69.85, 31.75) * mm});
            skLineSegment(sketch, "E207.0", {"start": v(63.5, -38.1) * mm, "end": v(-63.5, -38.1) * mm});
            skLineSegment(sketch, "E208.0", {"start": v(69.85, -31.75) * mm, "end": v(69.85, 31.75) * mm});
            skLineSegment(sketch, "E209", {"start": v(-12.7, 38.1) * mm, "end": v(-12.7, -38.1) * mm});
            skLineSegment(sketch, "E210", {"start": v(-25.4, 38.1) * mm, "end": v(-25.4, -38.1) * mm});
            skLineSegment(sketch, "E211", {"start": v(-38.1, 38.1) * mm, "end": v(-38.1, -38.1) * mm});
            skLineSegment(sketch, "E212", {"start": v(-50.8, 38.1) * mm, "end": v(-50.8, -38.1) * mm});
            skLineSegment(sketch, "E213", {"start": v(-69.85, 6.35) * mm, "end": v(69.85, 6.35) * mm});
            skLineSegment(sketch, "E214", {"start": v(-75.27, 0) * mm, "end": v(78.66, 0) * mm, "construction": true});
            skLineSegment(sketch, "E215", {"start": v(0, 56.55) * mm, "end": v(0, -47.98) * mm, "construction": true});
            skLineSegment(sketch, "E216.MirrorCS", {"start": v(-69.85, -6.35) * mm, "end": v(69.85, -6.35) * mm});
            skLineSegment(sketch, "E217.MirrorCS", {"start": v(12.7, 38.1) * mm, "end": v(12.7, -38.1) * mm});
            skLineSegment(sketch, "E218.MirrorCS", {"start": v(25.4, 38.1) * mm, "end": v(25.4, -38.1) * mm});
            skLineSegment(sketch, "E219.MirrorCS", {"start": v(38.1, 38.1) * mm, "end": v(38.1, -38.1) * mm});
            skLineSegment(sketch, "E220.MirrorCS", {"start": v(50.8, 38.1) * mm, "end": v(50.8, -38.1) * mm});
            skSolve(sketch);
        }
        {
            var Q0;
            {var subQ5=makeQuery(id+"F3.opExtrude","CAP_EDGE",EDGE,{"disambiguationData":[OSD([sQuery(id+"F2.wireOp",EDGE,"E7.4")])],"isStart":false});Q0=makeQuery(id+"F25.imprint","IMPRINT",FACE,{"disambiguationData":[TD([[makeQuery(id+"F25.imprint","IMPRINT",EDGE,{"derivedFrom":subQ5}),-1.0]])]});}
            var Q1;
            {var subQ0=sQuery(id+"F25.wireOp",EDGE,"E210");var subQ1=sQuery(id+"F25.wireOp",EDGE,"E205.0");var subQ2=makeQuery(id+"F25.imprint","INTERSECT",VERTEX,{"derivedFrom":[subQ1,subQ0]});Q1=makeQuery(id+"F25.imprint","IMPRINT",FACE,{"disambiguationData":[TD([[makeQuery(id+"F25.imprint","IMPRINT",EDGE,{"disambiguationData":[TD([[subQ2,-1.0]])],"derivedFrom":subQ1}),1.0]])]});}
            var Q2;
            {var subQ0=sQuery(id+"F25.wireOp",EDGE,"E209");var subQ1=sQuery(id+"F25.wireOp",EDGE,"E205.0");var subQ2=makeQuery(id+"F25.imprint","INTERSECT",VERTEX,{"derivedFrom":[subQ1,subQ0]});Q2=makeQuery(id+"F25.imprint","IMPRINT",FACE,{"disambiguationData":[TD([[makeQuery(id+"F25.imprint","IMPRINT",EDGE,{"disambiguationData":[TD([[subQ2,1.0]])],"derivedFrom":subQ1}),1.0]])]});}
            var Q3;
            {var subQ0=sQuery(id+"F25.wireOp",EDGE,"E218.MirrorCS");var subQ1=sQuery(id+"F25.wireOp",EDGE,"E205.0");var subQ2=makeQuery(id+"F25.imprint","INTERSECT",VERTEX,{"derivedFrom":[subQ1,subQ0]});Q3=makeQuery(id+"F25.imprint","IMPRINT",FACE,{"disambiguationData":[TD([[makeQuery(id+"F25.imprint","IMPRINT",EDGE,{"disambiguationData":[TD([[subQ2,1.0]])],"derivedFrom":subQ1}),1.0]])]});}
            var Q4;
            {var subQ11=makeQuery(id+"F3.opExtrude","CAP_EDGE",EDGE,{"disambiguationData":[OSD([sQuery(id+"F2.wireOp",EDGE,"E7.0")])],"isStart":false});Q4=makeQuery(id+"F25.imprint","IMPRINT",FACE,{"disambiguationData":[TD([[makeQuery(id+"F25.imprint","IMPRINT",EDGE,{"derivedFrom":subQ11}),-1.0]])]});}
            var Q5;
            {var subQ11=makeQuery(id+"F3.opExtrude","CAP_EDGE",EDGE,{"disambiguationData":[OSD([sQuery(id+"F2.wireOp",EDGE,"E7.3")])],"isStart":false});Q5=makeQuery(id+"F25.imprint","IMPRINT",FACE,{"disambiguationData":[TD([[makeQuery(id+"F25.imprint","IMPRINT",EDGE,{"derivedFrom":subQ11}),-1.0]])]});}
            var Q6;
            {var subQ0=sQuery(id+"F25.wireOp",EDGE,"E218.MirrorCS");var subQ1=sQuery(id+"F25.wireOp",EDGE,"E207.0");var subQ2=makeQuery(id+"F25.imprint","INTERSECT",VERTEX,{"derivedFrom":[subQ1,subQ0]});Q6=makeQuery(id+"F25.imprint","IMPRINT",FACE,{"disambiguationData":[TD([[makeQuery(id+"F25.imprint","IMPRINT",EDGE,{"disambiguationData":[TD([[subQ2,1.0]])],"derivedFrom":subQ1}),-1.0]])]});}
            var Q7;
            {var subQ0=sQuery(id+"F25.wireOp",EDGE,"E209");var subQ1=sQuery(id+"F25.wireOp",EDGE,"E207.0");var subQ2=makeQuery(id+"F25.imprint","INTERSECT",VERTEX,{"derivedFrom":[subQ1,subQ0]});Q7=makeQuery(id+"F25.imprint","IMPRINT",FACE,{"disambiguationData":[TD([[makeQuery(id+"F25.imprint","IMPRINT",EDGE,{"disambiguationData":[TD([[subQ2,1.0]])],"derivedFrom":subQ1}),-1.0]])]});}
            var Q8;
            {var subQ0=sQuery(id+"F25.wireOp",EDGE,"E210");var subQ1=sQuery(id+"F25.wireOp",EDGE,"E207.0");var subQ2=makeQuery(id+"F25.imprint","INTERSECT",VERTEX,{"derivedFrom":[subQ1,subQ0]});Q8=makeQuery(id+"F25.imprint","IMPRINT",FACE,{"disambiguationData":[TD([[makeQuery(id+"F25.imprint","IMPRINT",EDGE,{"disambiguationData":[TD([[subQ2,-1.0]])],"derivedFrom":subQ1}),-1.0]])]});}
            var Q9;
            {var subQ11=makeQuery(id+"F3.opExtrude","CAP_EDGE",EDGE,{"disambiguationData":[OSD([sQuery(id+"F2.wireOp",EDGE,"E7.6")])],"isStart":false});Q9=makeQuery(id+"F25.imprint","IMPRINT",FACE,{"disambiguationData":[TD([[makeQuery(id+"F25.imprint","IMPRINT",EDGE,{"derivedFrom":subQ11}),-1.0]])]});}
            var Q10;
            {var subQ0=sQuery(id+"F25.wireOp",EDGE,"E211");var subQ1=sQuery(id+"F25.wireOp",EDGE,"E205.0");var subQ2=makeQuery(id+"F25.imprint","INTERSECT",VERTEX,{"derivedFrom":[subQ1,subQ0]});Q10=makeQuery(id+"F25.imprint","IMPRINT",FACE,{"disambiguationData":[TD([[makeQuery(id+"F25.imprint","IMPRINT",EDGE,{"disambiguationData":[TD([[subQ2,-1.0]])],"derivedFrom":subQ1}),1.0]])]});}
            var Q11;
            {var subQ0=sQuery(id+"F25.wireOp",EDGE,"E219.MirrorCS");var subQ1=sQuery(id+"F25.wireOp",EDGE,"E205.0");var subQ2=makeQuery(id+"F25.imprint","INTERSECT",VERTEX,{"derivedFrom":[subQ1,subQ0]});Q11=makeQuery(id+"F25.imprint","IMPRINT",FACE,{"disambiguationData":[TD([[makeQuery(id+"F25.imprint","IMPRINT",EDGE,{"disambiguationData":[TD([[subQ2,1.0]])],"derivedFrom":subQ1}),1.0]])]});}
            var Q12;
            {var subQ0=sQuery(id+"F25.wireOp",EDGE,"E219.MirrorCS");var subQ1=sQuery(id+"F25.wireOp",EDGE,"E207.0");var subQ2=makeQuery(id+"F25.imprint","INTERSECT",VERTEX,{"derivedFrom":[subQ1,subQ0]});Q12=makeQuery(id+"F25.imprint","IMPRINT",FACE,{"disambiguationData":[TD([[makeQuery(id+"F25.imprint","IMPRINT",EDGE,{"disambiguationData":[TD([[subQ2,1.0]])],"derivedFrom":subQ1}),-1.0]])]});}
            var Q13;
            {var subQ0=sQuery(id+"F25.wireOp",EDGE,"E211");var subQ1=sQuery(id+"F25.wireOp",EDGE,"E207.0");var subQ2=makeQuery(id+"F25.imprint","INTERSECT",VERTEX,{"derivedFrom":[subQ1,subQ0]});Q13=makeQuery(id+"F25.imprint","IMPRINT",FACE,{"disambiguationData":[TD([[makeQuery(id+"F25.imprint","IMPRINT",EDGE,{"disambiguationData":[TD([[subQ2,-1.0]])],"derivedFrom":subQ1}),-1.0]])]});}
            extrude(context, id + "F26", {"entities" : qUnion([Q0, Q1, Q2, Q3, Q4, Q5, Q6, Q7, Q8, Q9, Q10, Q11, Q12, Q13]), "operationType" : NewBodyOperationType.REMOVE, "endBound" : BoundingType.THROUGH_ALL, "depth" : 25.4 * mm});
        }
        {
            var Q0;
            {var subQ0=sQuery(id+"F25.wireOp",EDGE,"E209");var subQ1=sQuery(id+"F25.wireOp",EDGE,"E205.0");var subQ2=makeQuery(id+"F25.imprint","INTERSECT",VERTEX,{"derivedFrom":[subQ1,subQ0]});Q0=makeQuery(id+"F25.imprint","IMPRINT",FACE,{"disambiguationData":[TD([[makeQuery(id+"F25.imprint","IMPRINT",EDGE,{"disambiguationData":[TD([[subQ2,-1.0]])],"derivedFrom":subQ1}),1.0]])]});}
            var Q1;
            {var subQ0=sQuery(id+"F25.wireOp",EDGE,"E217.MirrorCS");var subQ1=sQuery(id+"F25.wireOp",EDGE,"E205.0");var subQ2=makeQuery(id+"F25.imprint","INTERSECT",VERTEX,{"derivedFrom":[subQ1,subQ0]});Q1=makeQuery(id+"F25.imprint","IMPRINT",FACE,{"disambiguationData":[TD([[makeQuery(id+"F25.imprint","IMPRINT",EDGE,{"disambiguationData":[TD([[subQ2,1.0]])],"derivedFrom":subQ1}),1.0]])]});}
            var Q2;
            {var subQ0=sQuery(id+"F25.wireOp",EDGE,"E213");var subQ1=sQuery(id+"F25.wireOp",EDGE,"E206.0");var subQ2=makeQuery(id+"F25.imprint","INTERSECT",VERTEX,{"derivedFrom":[subQ1,subQ0]});Q2=makeQuery(id+"F25.imprint","IMPRINT",FACE,{"disambiguationData":[TD([[makeQuery(id+"F25.imprint","IMPRINT",EDGE,{"disambiguationData":[TD([[subQ2,1.0]])],"derivedFrom":subQ1}),-1.0]])]});}
            var Q3;
            {var subQ0=sQuery(id+"F25.wireOp",EDGE,"E209");var subQ1=sQuery(id+"F25.wireOp",EDGE,"E207.0");var subQ2=makeQuery(id+"F25.imprint","INTERSECT",VERTEX,{"derivedFrom":[subQ1,subQ0]});Q3=makeQuery(id+"F25.imprint","IMPRINT",FACE,{"disambiguationData":[TD([[makeQuery(id+"F25.imprint","IMPRINT",EDGE,{"disambiguationData":[TD([[subQ2,-1.0]])],"derivedFrom":subQ1}),-1.0]])]});}
            var Q4;
            {var subQ0=sQuery(id+"F25.wireOp",EDGE,"E217.MirrorCS");var subQ1=sQuery(id+"F25.wireOp",EDGE,"E207.0");var subQ2=makeQuery(id+"F25.imprint","INTERSECT",VERTEX,{"derivedFrom":[subQ1,subQ0]});Q4=makeQuery(id+"F25.imprint","IMPRINT",FACE,{"disambiguationData":[TD([[makeQuery(id+"F25.imprint","IMPRINT",EDGE,{"disambiguationData":[TD([[subQ2,1.0]])],"derivedFrom":subQ1}),-1.0]])]});}
            var Q5;
            {var subQ0=sQuery(id+"F25.wireOp",EDGE,"E213");var subQ1=sQuery(id+"F25.wireOp",EDGE,"E208.0");var subQ2=makeQuery(id+"F25.imprint","INTERSECT",VERTEX,{"derivedFrom":[subQ1,subQ0]});Q5=makeQuery(id+"F25.imprint","IMPRINT",FACE,{"disambiguationData":[TD([[makeQuery(id+"F25.imprint","IMPRINT",EDGE,{"disambiguationData":[TD([[subQ2,1.0]])],"derivedFrom":subQ1}),1.0]])]});}
            var Q6;
            {var subQ0=sQuery(id+"F25.wireOp",EDGE,"E218.MirrorCS");var subQ1=sQuery(id+"F25.wireOp",EDGE,"E207.0");var subQ2=makeQuery(id+"F25.imprint","INTERSECT",VERTEX,{"derivedFrom":[subQ1,subQ0]});Q6=makeQuery(id+"F25.imprint","IMPRINT",FACE,{"disambiguationData":[TD([[makeQuery(id+"F25.imprint","IMPRINT",EDGE,{"disambiguationData":[TD([[subQ2,1.0]])],"derivedFrom":subQ1}),-1.0]])]});}
            var Q7;
            {var subQ0=sQuery(id+"F25.wireOp",EDGE,"E209");var subQ1=sQuery(id+"F25.wireOp",EDGE,"E207.0");var subQ2=makeQuery(id+"F25.imprint","INTERSECT",VERTEX,{"derivedFrom":[subQ1,subQ0]});Q7=makeQuery(id+"F25.imprint","IMPRINT",FACE,{"disambiguationData":[TD([[makeQuery(id+"F25.imprint","IMPRINT",EDGE,{"disambiguationData":[TD([[subQ2,1.0]])],"derivedFrom":subQ1}),-1.0]])]});}
            var Q8;
            {var subQ0=sQuery(id+"F25.wireOp",EDGE,"E210");var subQ1=sQuery(id+"F25.wireOp",EDGE,"E207.0");var subQ2=makeQuery(id+"F25.imprint","INTERSECT",VERTEX,{"derivedFrom":[subQ1,subQ0]});Q8=makeQuery(id+"F25.imprint","IMPRINT",FACE,{"disambiguationData":[TD([[makeQuery(id+"F25.imprint","IMPRINT",EDGE,{"disambiguationData":[TD([[subQ2,-1.0]])],"derivedFrom":subQ1}),-1.0]])]});}
            var Q9;
            {var subQ0=sQuery(id+"F25.wireOp",EDGE,"E210");var subQ1=sQuery(id+"F25.wireOp",EDGE,"E205.0");var subQ2=makeQuery(id+"F25.imprint","INTERSECT",VERTEX,{"derivedFrom":[subQ1,subQ0]});Q9=makeQuery(id+"F25.imprint","IMPRINT",FACE,{"disambiguationData":[TD([[makeQuery(id+"F25.imprint","IMPRINT",EDGE,{"disambiguationData":[TD([[subQ2,-1.0]])],"derivedFrom":subQ1}),1.0]])]});}
            var Q10;
            {var subQ0=sQuery(id+"F25.wireOp",EDGE,"E209");var subQ1=sQuery(id+"F25.wireOp",EDGE,"E205.0");var subQ2=makeQuery(id+"F25.imprint","INTERSECT",VERTEX,{"derivedFrom":[subQ1,subQ0]});Q10=makeQuery(id+"F25.imprint","IMPRINT",FACE,{"disambiguationData":[TD([[makeQuery(id+"F25.imprint","IMPRINT",EDGE,{"disambiguationData":[TD([[subQ2,1.0]])],"derivedFrom":subQ1}),1.0]])]});}
            var Q11;
            {var subQ0=sQuery(id+"F25.wireOp",EDGE,"E218.MirrorCS");var subQ1=sQuery(id+"F25.wireOp",EDGE,"E205.0");var subQ2=makeQuery(id+"F25.imprint","INTERSECT",VERTEX,{"derivedFrom":[subQ1,subQ0]});Q11=makeQuery(id+"F25.imprint","IMPRINT",FACE,{"disambiguationData":[TD([[makeQuery(id+"F25.imprint","IMPRINT",EDGE,{"disambiguationData":[TD([[subQ2,1.0]])],"derivedFrom":subQ1}),1.0]])]});}
            var Q12;
            Q12=makeQuery(id+"F1.opExtrude","CAP_FACE",FACE,{"disambiguationData":[OSD([sQuery(id+"F0.wireOp",EDGE,"E2.bottom"),sQuery(id+"F0.wireOp",EDGE,"E2.top"),sQuery(id+"F0.wireOp",EDGE,"E2.left"),sQuery(id+"F0.wireOp",EDGE,"E2.right"),sQuery(id+"F0.wireOp",EDGE,"E3.filletArc"),sQuery(id+"F0.wireOp",EDGE,"E4.filletArc"),sQuery(id+"F0.wireOp",EDGE,"E5.filletArc"),sQuery(id+"F0.wireOp",EDGE,"E6.filletArc")])],"isStart":false});
            extrude(context, id + "F27", {"entities" : qUnion([Q0, Q1, Q2, Q3, Q4, Q5, Q6, Q7, Q8, Q9, Q10, Q11]), "operationType" : NewBodyOperationType.REMOVE, "endBound" : BoundingType.UP_TO_SURFACE, "oppositeDirection" : true, "endBoundEntityFace" : qUnion([Q12]), "depth" : 25.4 * mm});
        }
    });
